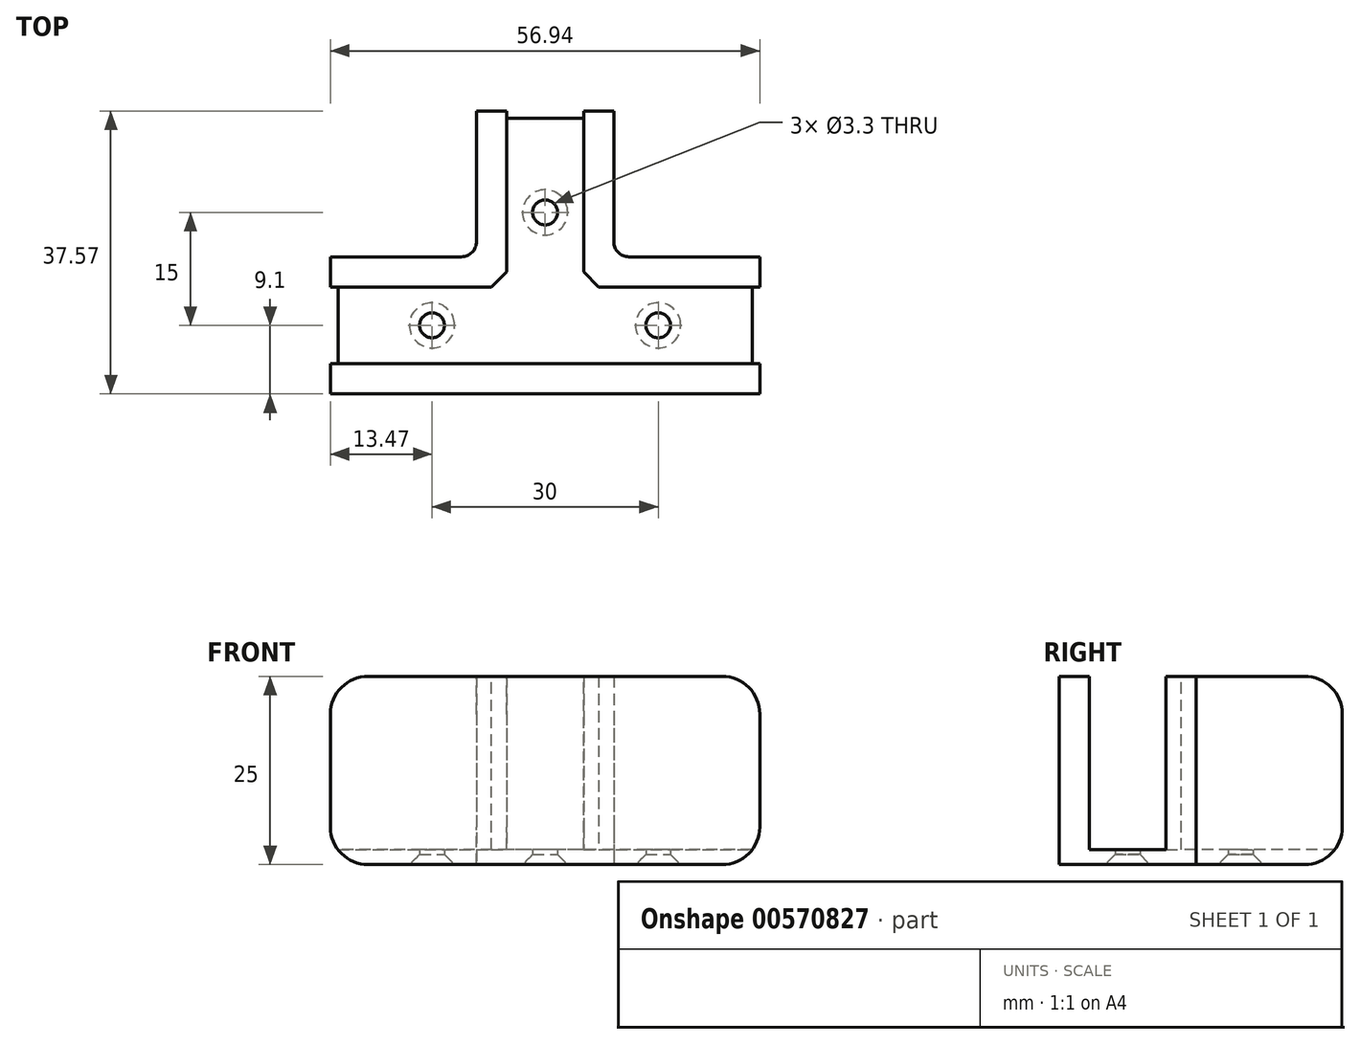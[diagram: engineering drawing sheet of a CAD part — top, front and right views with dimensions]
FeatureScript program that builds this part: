
annotation { "Feature Type Name" : "Feature", "Feature Type Description" : "" }
export const myFeature = defineFeature(function(context is Context, id is Id, definition is map)
    precondition{}
    {
        {
            var Q0;
            Q0=qCreatedBy(makeId("Top.planeOp"),FACE);
            var sketch = newSketch(context, id + "F0", { "sketchPlane" : qUnion([Q0])});
            skLineSegment(sketch, "E0", {"start": v(0, 0) * mm, "end": v(28.47, 0) * mm});
            skLineSegment(sketch, "E1", {"start": v(28.47, 10.2) * mm, "end": v(5.1, 10.2) * mm});
            skLineSegment(sketch, "E2", {"start": v(5.1, 10.2) * mm, "end": v(5.1, 33.57) * mm});
            skLineSegment(sketch, "E3", {"start": v(-5.1, 33.57) * mm, "end": v(-5.1, 10.2) * mm});
            skLineSegment(sketch, "E4", {"start": v(-5.1, 10.2) * mm, "end": v(-28.47, 10.2) * mm});
            skLineSegment(sketch, "E5", {"start": v(-28.47, 0) * mm, "end": v(0, 0) * mm});
            skLineSegment(sketch, "E6.0", {"start": v(9.1, 33.57) * mm, "end": v(-9.1, 33.57) * mm});
            skLineSegment(sketch, "E6.1", {"start": v(9.1, 14.2) * mm, "end": v(9.1, 33.57) * mm});
            skLineSegment(sketch, "E6.2", {"start": v(-9.1, 33.57) * mm, "end": v(-9.1, 14.2) * mm});
            skLineSegment(sketch, "E6.3", {"start": v(28.47, 14.2) * mm, "end": v(9.1, 14.2) * mm});
            skLineSegment(sketch, "E6.4", {"start": v(28.47, -4) * mm, "end": v(28.47, 14.2) * mm});
            skLineSegment(sketch, "E6.5", {"start": v(-9.1, 14.2) * mm, "end": v(-28.47, 14.2) * mm});
            skLineSegment(sketch, "E6.6", {"start": v(-28.47, 14.2) * mm, "end": v(-28.47, -4) * mm});
            skLineSegment(sketch, "E6.7", {"start": v(-28.47, -4) * mm, "end": v(0, -4) * mm});
            skLineSegment(sketch, "E6.8", {"start": v(0, -4) * mm, "end": v(28.47, -4) * mm});
            skPoint(sketch, "E7", {"position": v(0, 33.57) * mm});
            skSolve(sketch);
        }
        {
            var Q0;
            Q0=qSketchRegion(id+"F0",true);
            extrude(context, id + "F1", {"entities" : qUnion([Q0]), "depth" : 2 * mm, "offsetDistance" : 25 * mm});
        }
        {
            var Q0;
            {var subQ4=sQuery(id+"F0.wireOp",EDGE,"E3");Q0=makeQuery(id+"F0.imprint","IMPRINT",FACE,{"disambiguationData":[TD([[makeQuery(id+"F0.imprint","IMPRINT",EDGE,{"derivedFrom":subQ4}),-1.0]])]});}
            var Q1;
            {var subQ3=sQuery(id+"F0.wireOp",EDGE,"E1");Q1=makeQuery(id+"F0.imprint","IMPRINT",FACE,{"disambiguationData":[TD([[makeQuery(id+"F0.imprint","IMPRINT",EDGE,{"derivedFrom":subQ3}),-1.0]])]});}
            var Q2;
            {var subQ4=sQuery(id+"F0.wireOp",EDGE,"E0");Q2=makeQuery(id+"F0.imprint","IMPRINT",FACE,{"disambiguationData":[TD([[makeQuery(id+"F0.imprint","IMPRINT",EDGE,{"derivedFrom":subQ4}),-1.0]])]});}
            extrude(context, id + "F2", {"entities" : qUnion([Q0, Q1, Q2]), "operationType" : NewBodyOperationType.ADD, "depth" : 25 * mm, "offsetDistance" : 25 * mm});
        }
        {
            var Q0;
            {var subQ0=sQuery(id+"F0.wireOp",EDGE,"E6.3");var subQ1=sQuery(id+"F0.wireOp",EDGE,"E6.1");Q0=makeQuery(id+"F2.boolean.opBoolean","MERGE",EDGE,{"derivedFrom":[makeQuery(id+"F1.opExtrude","SWEPT_EDGE",EDGE,{"disambiguationData":[OSD([subQ1,subQ0])]}),makeQuery(id+"F2.opExtrude","SWEPT_EDGE",EDGE,{"disambiguationData":[OSD([subQ1,subQ0])]})]});}
            fillet(context, id + "F3", {"entities" : qUnion([Q0]), "radius" : 2 * mm, "tangentPropagation" : true, "allowEdgeOverflow" : false});
        }
        {
            var Q0;
            {var subQ0=sQuery(id+"F0.wireOp",EDGE,"E6.4");Q0=makeQuery(id+"F2.opExtrude","CAP_EDGE",EDGE,{"disambiguationData":[OSD([subQ0]),TDD([makeQuery(id+"F0.imprint","IMPRINT",EDGE,{"disambiguationData":[TD([[makeQuery(id+"F0.imprint","INTERSECT",VERTEX,{"derivedFrom":[sQuery(id+"F0.wireOp",EDGE,"E0"),subQ0]}),1.0]])],"derivedFrom":subQ0})])],"isStart":false});}
            var Q1;
            {var subQ0=sQuery(id+"F0.wireOp",EDGE,"E6.4");Q1=makeQuery(id+"F2.opExtrude","CAP_EDGE",EDGE,{"disambiguationData":[OSD([subQ0]),TDD([makeQuery(id+"F0.imprint","IMPRINT",EDGE,{"disambiguationData":[TD([[makeQuery(id+"F0.imprint","INTERSECT",VERTEX,{"derivedFrom":[sQuery(id+"F0.wireOp",EDGE,"E1"),subQ0]}),-1.0]])],"derivedFrom":subQ0})])],"isStart":false});}
            var Q2;
            {var subQ0=sQuery(id+"F0.wireOp",EDGE,"E6.6");Q2=makeQuery(id+"F2.opExtrude","CAP_EDGE",EDGE,{"disambiguationData":[OSD([subQ0]),TDD([makeQuery(id+"F0.imprint","IMPRINT",EDGE,{"disambiguationData":[TD([[makeQuery(id+"F0.imprint","INTERSECT",VERTEX,{"derivedFrom":[sQuery(id+"F0.wireOp",EDGE,"E5"),subQ0]}),-1.0]])],"derivedFrom":subQ0})])],"isStart":false});}
            var Q3;
            {var subQ0=sQuery(id+"F0.wireOp",EDGE,"E6.6");Q3=makeQuery(id+"F2.opExtrude","CAP_EDGE",EDGE,{"disambiguationData":[OSD([subQ0]),TDD([makeQuery(id+"F0.imprint","IMPRINT",EDGE,{"disambiguationData":[TD([[makeQuery(id+"F0.imprint","INTERSECT",VERTEX,{"derivedFrom":[sQuery(id+"F0.wireOp",EDGE,"E4"),subQ0]}),1.0]])],"derivedFrom":subQ0})])],"isStart":false});}
            var Q4;
            {var subQ0=sQuery(id+"F0.wireOp",EDGE,"E6.0");Q4=makeQuery(id+"F2.opExtrude","CAP_EDGE",EDGE,{"disambiguationData":[OSD([subQ0]),TDD([makeQuery(id+"F0.imprint","IMPRINT",EDGE,{"disambiguationData":[TD([[makeQuery(id+"F0.imprint","INTERSECT",VERTEX,{"derivedFrom":[sQuery(id+"F0.wireOp",EDGE,"E3"),subQ0]}),-1.0]])],"derivedFrom":subQ0})])],"isStart":false});}
            var Q5;
            {var subQ0=sQuery(id+"F0.wireOp",EDGE,"E6.0");Q5=makeQuery(id+"F2.opExtrude","CAP_EDGE",EDGE,{"disambiguationData":[OSD([subQ0]),TDD([makeQuery(id+"F0.imprint","IMPRINT",EDGE,{"disambiguationData":[TD([[makeQuery(id+"F0.imprint","INTERSECT",VERTEX,{"derivedFrom":[sQuery(id+"F0.wireOp",EDGE,"E2"),subQ0]}),1.0]])],"derivedFrom":subQ0})])],"isStart":false});}
            var Q6;
            Q6=makeQuery(id+"F1.opExtrude","CAP_EDGE",EDGE,{"disambiguationData":[OSD([sQuery(id+"F0.wireOp",EDGE,"E6.6")])],"isStart":true});
            var Q7;
            Q7=makeQuery(id+"F1.opExtrude","CAP_EDGE",EDGE,{"disambiguationData":[OSD([sQuery(id+"F0.wireOp",EDGE,"E6.4")])],"isStart":true});
            var Q8;
            Q8=makeQuery(id+"F1.opExtrude","CAP_EDGE",EDGE,{"disambiguationData":[OSD([sQuery(id+"F0.wireOp",EDGE,"E6.0")])],"isStart":true});
            fillet(context, id + "F4", {"entities" : qUnion([Q0, Q1, Q2, Q3, Q4, Q5, Q6, Q7, Q8]), "radius" : 5 * mm, "tangentPropagation" : true, "allowEdgeOverflow" : false});
        }
        {
            var Q0;
            {var subQ0=sQuery(id+"F0.wireOp",EDGE,"E6.5");var subQ1=sQuery(id+"F0.wireOp",EDGE,"E6.2");Q0=makeQuery(id+"F2.boolean.opBoolean","MERGE",EDGE,{"derivedFrom":[makeQuery(id+"F1.opExtrude","SWEPT_EDGE",EDGE,{"disambiguationData":[OSD([subQ1,subQ0])]}),makeQuery(id+"F2.opExtrude","SWEPT_EDGE",EDGE,{"disambiguationData":[OSD([subQ1,subQ0])]})]});}
            fillet(context, id + "F5", {"entities" : qUnion([Q0]), "radius" : 2 * mm, "tangentPropagation" : true, "allowEdgeOverflow" : false});
        }
        {
            var Q0;
            Q0=makeQuery(id+"F2.opExtrude","SWEPT_EDGE",EDGE,{"disambiguationData":[OSD([sQuery(id+"F0.wireOp",EDGE,"E1"),sQuery(id+"F0.wireOp",EDGE,"E2")])]});
            var Q1;
            Q1=makeQuery(id+"F2.opExtrude","SWEPT_EDGE",EDGE,{"disambiguationData":[OSD([sQuery(id+"F0.wireOp",EDGE,"E3"),sQuery(id+"F0.wireOp",EDGE,"E4")])]});
            chamfer(context, id + "F6", {"entities" : qUnion([Q0, Q1]), "width" : 2 * mm, "tangentPropagation" : true});
        }
        {
            var Q0;
            {var subQ3=sQuery(id+"F0.wireOp",EDGE,"E0");Q0=makeQuery(id+"F0.imprint","IMPRINT",FACE,{"disambiguationData":[TD([[makeQuery(id+"F0.imprint","IMPRINT",EDGE,{"derivedFrom":subQ3}),1.0]])]});}
            var sketch = newSketch(context, id + "F7", { "sketchPlane" : qUnion([Q0])});
            skLineSegment(sketch, "E8", {"start": v(-23.47, 5.1) * mm, "end": v(23.47, 5.1) * mm});
            skPoint(sketch, "E9", {"position": v(-15, 5.1) * mm});
            skPoint(sketch, "E10", {"position": v(15, 5.1) * mm});
            skPoint(sketch, "E11", {"position": v(0, 20.1) * mm});
            skSolve(sketch);
        }
        {
            var Q0;
            Q0=sQuery(id+"F7.wireOp",VERTEX,"E9");
            var Q1;
            Q1=sQuery(id+"F7.wireOp",VERTEX,"E11");
            var Q2;
            Q2=sQuery(id+"F7.wireOp",VERTEX,"E10");
            var Q3;
            Q3=makeQuery(id+"F1.opExtrude","SWEPT_BODY",BODY,{"disambiguationData":[OSD([sQuery(id+"F0.wireOp",EDGE,"E6.0"),sQuery(id+"F0.wireOp",EDGE,"E6.1"),sQuery(id+"F0.wireOp",EDGE,"E6.2"),sQuery(id+"F0.wireOp",EDGE,"E6.3"),sQuery(id+"F0.wireOp",EDGE,"E6.4"),sQuery(id+"F0.wireOp",EDGE,"E6.5"),sQuery(id+"F0.wireOp",EDGE,"E6.6"),sQuery(id+"F0.wireOp",EDGE,"E6.7"),sQuery(id+"F0.wireOp",EDGE,"E6.8")])]});
            hole(context, id + "F8", {"style" : HoleStyle.C_SINK, "endStyle" : HoleEndStyle.THROUGH, "oppositeDirection" : true, "holeDiameter" : 3.3 * mm, "cSinkDiameter" : 6 * mm, "cSinkAngle" : 90 * degree, "majorDiameter" : 5 * mm, "isTappedThrough" : true, "tappedDepth" : 12 * mm, "tapClearance" : 3, "locations" : qUnion([Q0, Q1, Q2]), "scope" : qUnion([Q3])});
        }
    });
